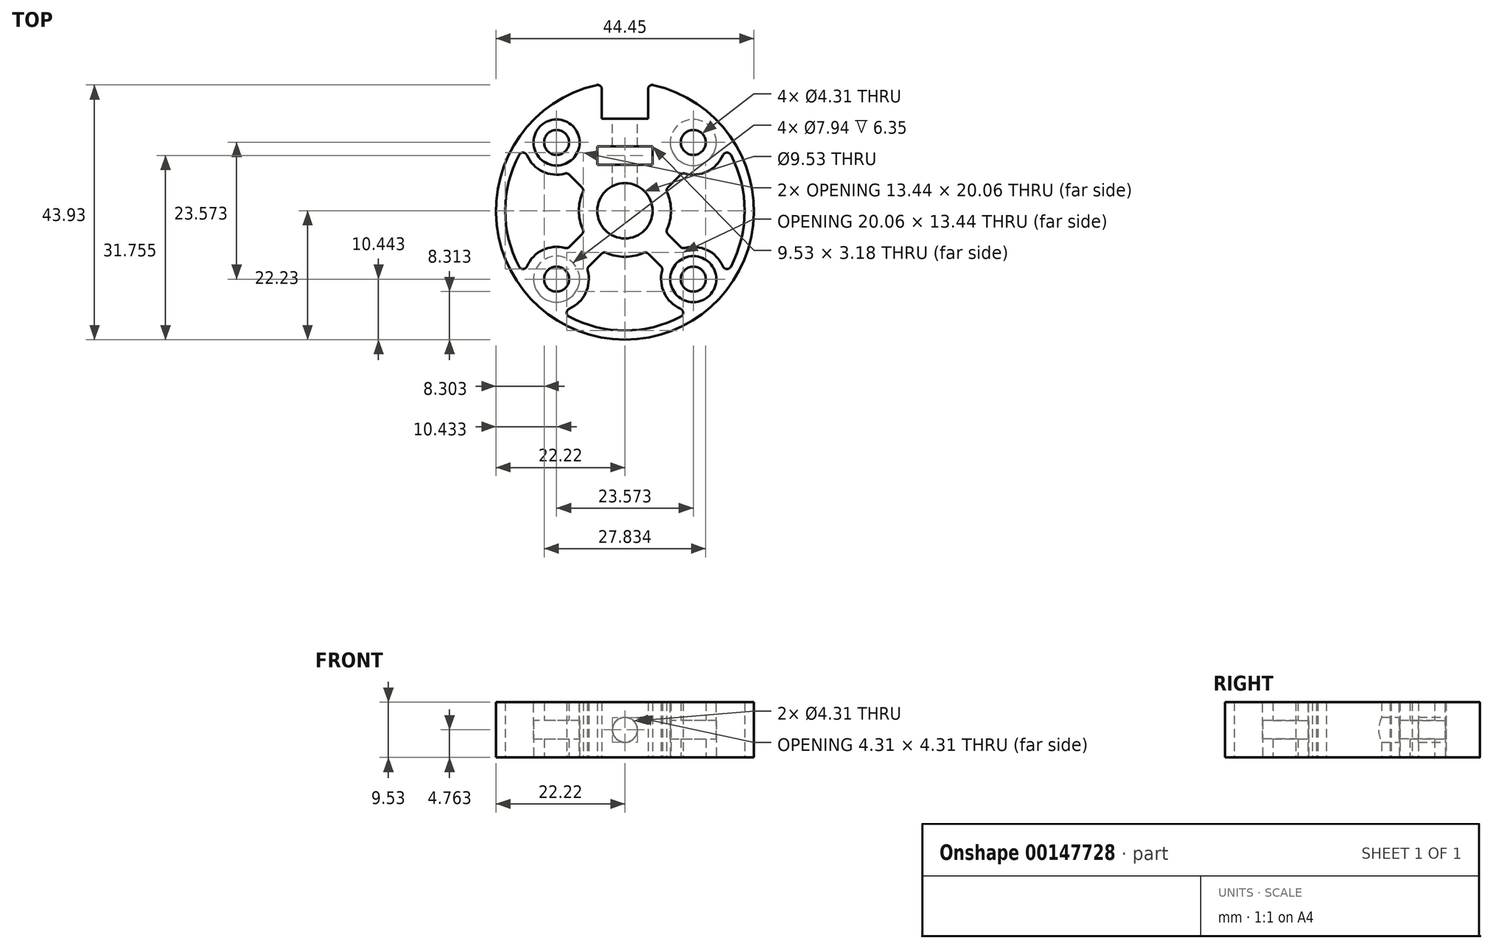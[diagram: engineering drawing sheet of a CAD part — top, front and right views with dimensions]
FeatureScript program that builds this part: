
annotation { "Feature Type Name" : "Feature", "Feature Type Description" : "" }
export const myFeature = defineFeature(function(context is Context, id is Id, definition is map)
    precondition{}
    {
        {
            var Q0;
            Q0=qCreatedBy(makeId("Top.planeOp"),FACE);
            var sketch = newSketch(context, id + "F0", { "sketchPlane" : qUnion([Q0])});
            skCircle(sketch, "E0", {"center": v(0, 0) * mm, "radius": 4.76 * mm});
            skLineSegment(sketch, "E1.bottom", {"start": v(11.79, 11.79) * mm, "end": v(-11.79, 11.79) * mm, "construction": true});
            skLineSegment(sketch, "E1.top", {"start": v(11.79, -11.79) * mm, "end": v(-11.79, -11.79) * mm, "construction": true});
            skLineSegment(sketch, "E1.left", {"start": v(11.79, 11.79) * mm, "end": v(11.79, -11.79) * mm, "construction": true});
            skLineSegment(sketch, "E1.right", {"start": v(-11.79, 11.79) * mm, "end": v(-11.79, -11.79) * mm, "construction": true});
            skCircle(sketch, "E2", {"center": v(-11.79, 11.79) * mm, "radius": 5.56 * mm, "construction": true});
            skLineSegment(sketch, "E3.bottom", {"start": v(-3.97, 21.87) * mm, "end": v(3.97, 21.87) * mm, "construction": true});
            skLineSegment(sketch, "E3.top", {"start": v(-3.97, 15.87) * mm, "end": v(3.97, 15.88) * mm});
            skLineSegment(sketch, "E3.left", {"start": v(-3.97, 21.87) * mm, "end": v(-3.97, 15.88) * mm});
            skLineSegment(sketch, "E3.right", {"start": v(3.97, 21.87) * mm, "end": v(3.97, 15.88) * mm});
            skArc(sketch, "E4", {"start": v(-3.97, 21.87) * mm, "mid": v(0, -22.22) * mm, "end": v(3.97, 21.87) * mm});
            skCircle(sketch, "E5", {"center": v(-11.79, 11.79) * mm, "radius": 2.15 * mm});
            skCircle(sketch, "E6", {"center": v(-11.79, -11.79) * mm, "radius": 2.15 * mm});
            skCircle(sketch, "E7", {"center": v(11.79, -11.79) * mm, "radius": 2.15 * mm});
            skCircle(sketch, "E8", {"center": v(11.79, 11.79) * mm, "radius": 2.15 * mm});
            skLineSegment(sketch, "E9", {"start": v(0, 15.88) * mm, "end": v(0, 11.11) * mm, "construction": true});
            skLineSegment(sketch, "E10", {"start": v(0, 0) * mm, "end": v(0, 3.17) * mm, "construction": true});
            skLineSegment(sketch, "E11", {"start": v(0, 3.17) * mm, "end": v(0, 4.76) * mm, "construction": true});
            skLineSegment(sketch, "E12", {"start": v(0, 4.76) * mm, "end": v(0, 7.94) * mm, "construction": true});
            skLineSegment(sketch, "E13.bottom", {"start": v(4.76, 11.11) * mm, "end": v(-4.76, 11.11) * mm});
            skLineSegment(sketch, "E13.top", {"start": v(4.76, 7.94) * mm, "end": v(-4.76, 7.94) * mm});
            skLineSegment(sketch, "E13.left", {"start": v(4.76, 11.11) * mm, "end": v(4.76, 7.94) * mm});
            skLineSegment(sketch, "E13.right", {"start": v(-4.76, 11.11) * mm, "end": v(-4.76, 7.94) * mm});
            skSolve(sketch);
        }
        {
            var Q0;
            Q0=qSketchRegion(id+"F0",true);
            extrude(context, id + "F1", {"entities" : qUnion([Q0]), "depth" : 9.52 * mm});
        }
        {
            var Q0;
            Q0=makeQuery(id+"F1.opExtrude","SWEPT_FACE",FACE,{"disambiguationData":[OSD([sQuery(id+"F0.wireOp",EDGE,"E3.top")])]});
            var sketch = newSketch(context, id + "F2", { "sketchPlane" : qUnion([Q0])});
            skLineSegment(sketch, "E14", {"start": v(0, 9.53) * mm, "end": v(0, 0) * mm, "construction": true});
            skCircle(sketch, "E15", {"center": v(0, 4.76) * mm, "radius": 2.15 * mm});
            skSolve(sketch);
        }
        {
            var Q0;
            Q0=qSketchRegion(id+"F2",true);
            var Q1;
            Q1=makeQuery(id+"F1.opExtrude","SWEPT_FACE",FACE,{"disambiguationData":[OSD([sQuery(id+"F0.wireOp",EDGE,"E0")])]});
            extrude(context, id + "F3", {"entities" : qUnion([Q0]), "operationType" : NewBodyOperationType.REMOVE, "endBound" : BoundingType.UP_TO_SURFACE, "oppositeDirection" : true, "endBoundEntityFace" : qUnion([Q1]), "depth" : 25.4 * mm});
        }
        {
            var Q0;
            Q0=makeQuery(id+"F1.opExtrude","CAP_FACE",FACE,{"disambiguationData":[OSD([sQuery(id+"F0.wireOp",EDGE,"E0"),sQuery(id+"F0.wireOp",EDGE,"E3.top"),sQuery(id+"F0.wireOp",EDGE,"E3.left"),sQuery(id+"F0.wireOp",EDGE,"E3.right"),sQuery(id+"F0.wireOp",EDGE,"E4"),sQuery(id+"F0.wireOp",EDGE,"E5"),sQuery(id+"F0.wireOp",EDGE,"E6"),sQuery(id+"F0.wireOp",EDGE,"E7"),sQuery(id+"F0.wireOp",EDGE,"E8")])],"isStart":true});
            cPlane(context, id + "F4", {"entities" : qUnion([Q0]), "cplaneType" : CPlaneType.OFFSET, "offset" : 3.17 * mm, "oppositeDirection" : true, "width" : 152.4 * mm, "height" : 152.4 * mm});
        }
        {
            var Q0;
            Q0=makeQuery(id+"F1.opExtrude","CAP_FACE",FACE,{"disambiguationData":[OSD([sQuery(id+"F0.wireOp",EDGE,"E0"),sQuery(id+"F0.wireOp",EDGE,"E3.top"),sQuery(id+"F0.wireOp",EDGE,"E3.left"),sQuery(id+"F0.wireOp",EDGE,"E3.right"),sQuery(id+"F0.wireOp",EDGE,"E4"),sQuery(id+"F0.wireOp",EDGE,"E5"),sQuery(id+"F0.wireOp",EDGE,"E6"),sQuery(id+"F0.wireOp",EDGE,"E7"),sQuery(id+"F0.wireOp",EDGE,"E8")])],"isStart":false});
            cPlane(context, id + "F5", {"entities" : qUnion([Q0]), "cplaneType" : CPlaneType.OFFSET, "offset" : 3.17 * mm, "oppositeDirection" : true, "width" : 152.4 * mm, "height" : 152.4 * mm});
        }
        {
            var Q0;
            Q0=makeQuery(id+"F1.opExtrude","CAP_FACE",FACE,{"disambiguationData":[OSD([sQuery(id+"F0.wireOp",EDGE,"E0"),sQuery(id+"F0.wireOp",EDGE,"E3.top"),sQuery(id+"F0.wireOp",EDGE,"E3.left"),sQuery(id+"F0.wireOp",EDGE,"E3.right"),sQuery(id+"F0.wireOp",EDGE,"E4"),sQuery(id+"F0.wireOp",EDGE,"E5"),sQuery(id+"F0.wireOp",EDGE,"E6"),sQuery(id+"F0.wireOp",EDGE,"E7"),sQuery(id+"F0.wireOp",EDGE,"E8")])],"isStart":true});
            var sketch = newSketch(context, id + "F6", { "sketchPlane" : qUnion([Q0])});
            skCircle(sketch, "E16", {"center": v(11.79, -11.79) * mm, "radius": 3.97 * mm});
            skCircle(sketch, "E17", {"center": v(-11.79, 11.79) * mm, "radius": 3.97 * mm});
            skSolve(sketch);
        }
        {
            var Q0;
            Q0=qSketchRegion(id+"F6",true);
            var Q1;
            Q1=qCreatedBy(id+"F5.planeOp",FACE);
            extrude(context, id + "F7", {"entities" : qUnion([Q0]), "operationType" : NewBodyOperationType.REMOVE, "endBound" : BoundingType.UP_TO_SURFACE, "oppositeDirection" : true, "endBoundEntityFace" : qUnion([Q1]), "depth" : 25.4 * mm});
        }
        {
            var Q0;
            Q0=makeQuery(id+"F1.opExtrude","CAP_FACE",FACE,{"disambiguationData":[OSD([sQuery(id+"F0.wireOp",EDGE,"E0"),sQuery(id+"F0.wireOp",EDGE,"E3.top"),sQuery(id+"F0.wireOp",EDGE,"E3.left"),sQuery(id+"F0.wireOp",EDGE,"E3.right"),sQuery(id+"F0.wireOp",EDGE,"E4"),sQuery(id+"F0.wireOp",EDGE,"E5"),sQuery(id+"F0.wireOp",EDGE,"E6"),sQuery(id+"F0.wireOp",EDGE,"E7"),sQuery(id+"F0.wireOp",EDGE,"E8")])],"isStart":true});
            var sketch = newSketch(context, id + "F8", { "sketchPlane" : qUnion([Q0])});
            skArc(sketch, "E18", {"start": v(-9.92, -6.55) * mm, "mid": v(-14.76, -7.1) * mm, "end": v(-17.31, -11.23) * mm});
            skArc(sketch, "E19", {"start": v(-17.31, 11.23) * mm, "mid": v(-14.76, 7.1) * mm, "end": v(-9.92, 6.55) * mm});
            skArc(sketch, "E20", {"start": v(-17.31, 11.23) * mm, "mid": v(-20.64, 0) * mm, "end": v(-17.31, -11.23) * mm});
            skLineSegment(sketch, "E21", {"start": v(-11.79, 11.79) * mm, "end": v(-8.24, 8.24) * mm, "construction": true});
            skLineSegment(sketch, "E22", {"start": v(-11.79, -11.79) * mm, "end": v(-8.24, -8.24) * mm, "construction": true});
            skLineSegment(sketch, "E23", {"start": v(0, 0) * mm, "end": v(-5.35, 5.35) * mm, "construction": true});
            skLineSegment(sketch, "E24", {"start": v(0, 0) * mm, "end": v(-5.35, -5.35) * mm, "construction": true});
            skLineSegment(sketch, "E25.bottom", {"start": v(-7.04, 3.67) * mm, "end": v(-9.92, 6.55) * mm});
            skLineSegment(sketch, "E25.top", {"start": v(-3.67, 7.04) * mm, "end": v(-6.55, 9.92) * mm, "construction": true});
            skLineSegment(sketch, "E25.left", {"start": v(-7.04, 3.67) * mm, "end": v(-3.67, 7.04) * mm, "construction": true});
            skLineSegment(sketch, "E25.right", {"start": v(-9.92, 6.55) * mm, "end": v(-6.55, 9.92) * mm, "construction": true});
            skLineSegment(sketch, "E26.bottom", {"start": v(-7.04, -3.67) * mm, "end": v(-9.92, -6.55) * mm});
            skLineSegment(sketch, "E26.top", {"start": v(-3.67, -7.04) * mm, "end": v(-6.55, -9.92) * mm, "construction": true});
            skLineSegment(sketch, "E26.left", {"start": v(-7.04, -3.67) * mm, "end": v(-3.67, -7.04) * mm, "construction": true});
            skLineSegment(sketch, "E26.right", {"start": v(-9.92, -6.55) * mm, "end": v(-6.55, -9.92) * mm, "construction": true});
            skArc(sketch, "E27", {"start": v(-7.04, 3.67) * mm, "mid": v(-7.94, 0) * mm, "end": v(-7.04, -3.67) * mm});
            skSolve(sketch);
        }
        {
            var Q0;
            Q0=qSketchRegion(id+"F8",true);
            var Q1;
            Q1=makeQuery(id+"F1.opExtrude","CAP_FACE",FACE,{"disambiguationData":[OSD([sQuery(id+"F0.wireOp",EDGE,"E0"),sQuery(id+"F0.wireOp",EDGE,"E3.top"),sQuery(id+"F0.wireOp",EDGE,"E3.left"),sQuery(id+"F0.wireOp",EDGE,"E3.right"),sQuery(id+"F0.wireOp",EDGE,"E4"),sQuery(id+"F0.wireOp",EDGE,"E5"),sQuery(id+"F0.wireOp",EDGE,"E6"),sQuery(id+"F0.wireOp",EDGE,"E7"),sQuery(id+"F0.wireOp",EDGE,"E8")])],"isStart":false});
            extrude(context, id + "F9", {"entities" : qUnion([Q0]), "operationType" : NewBodyOperationType.REMOVE, "endBound" : BoundingType.UP_TO_SURFACE, "oppositeDirection" : true, "endBoundEntityFace" : qUnion([Q1]), "depth" : 25.4 * mm});
        }
        {
            var Q0;
            Q0=makeQuery(id+"F9.boolean.opBoolean","COPY",EDGE,{"derivedFrom":makeQuery(id+"F9.opExtrude","SWEPT_EDGE",EDGE,{"disambiguationData":[OSD([sQuery(id+"F8.wireOp",EDGE,"E19"),sQuery(id+"F8.wireOp",EDGE,"E20")])]})});
            var Q1;
            Q1=makeQuery(id+"F9.boolean.opBoolean","COPY",EDGE,{"derivedFrom":makeQuery(id+"F9.opExtrude","SWEPT_EDGE",EDGE,{"disambiguationData":[OSD([sQuery(id+"F8.wireOp",EDGE,"E19"),sQuery(id+"F8.wireOp",EDGE,"E25.bottom")])]})});
            var Q2;
            Q2=makeQuery(id+"F9.boolean.opBoolean","COPY",EDGE,{"derivedFrom":makeQuery(id+"F9.opExtrude","SWEPT_EDGE",EDGE,{"disambiguationData":[OSD([sQuery(id+"F8.wireOp",EDGE,"E25.bottom"),sQuery(id+"F8.wireOp",EDGE,"E27")])]})});
            var Q3;
            Q3=makeQuery(id+"F9.boolean.opBoolean","COPY",EDGE,{"derivedFrom":makeQuery(id+"F9.opExtrude","SWEPT_EDGE",EDGE,{"disambiguationData":[OSD([sQuery(id+"F8.wireOp",EDGE,"E26.bottom"),sQuery(id+"F8.wireOp",EDGE,"E27")])]})});
            var Q4;
            Q4=makeQuery(id+"F9.boolean.opBoolean","COPY",EDGE,{"derivedFrom":makeQuery(id+"F9.opExtrude","SWEPT_EDGE",EDGE,{"disambiguationData":[OSD([sQuery(id+"F8.wireOp",EDGE,"E18"),sQuery(id+"F8.wireOp",EDGE,"E26.bottom")])]})});
            var Q5;
            Q5=makeQuery(id+"F9.boolean.opBoolean","COPY",EDGE,{"derivedFrom":makeQuery(id+"F9.opExtrude","SWEPT_EDGE",EDGE,{"disambiguationData":[OSD([sQuery(id+"F8.wireOp",EDGE,"E18"),sQuery(id+"F8.wireOp",EDGE,"E20")])]})});
            var Q6;
            Q6=makeQuery(id+"F1.opExtrude","SWEPT_EDGE",EDGE,{"disambiguationData":[OSD([sQuery(id+"F0.wireOp",EDGE,"E3.right"),sQuery(id+"F0.wireOp",EDGE,"E4")])]});
            var Q7;
            Q7=makeQuery(id+"F1.opExtrude","SWEPT_EDGE",EDGE,{"disambiguationData":[OSD([sQuery(id+"F0.wireOp",EDGE,"E3.left"),sQuery(id+"F0.wireOp",EDGE,"E4")])]});
            fillet(context, id + "F10", {"entities" : qUnion([Q0, Q1, Q2, Q3, Q4, Q5, Q6, Q7]), "radius" : 0.76 * mm, "tangentPropagation" : true, "allowEdgeOverflow" : false});
        }
        {
            var Q0;
            Q0=makeQuery(id+"F10.opFillet","BLEND_FACE",FACE,{"disambiguationData":[OSD([sQuery(id+"F8.wireOp",EDGE,"E19"),sQuery(id+"F8.wireOp",EDGE,"E25.bottom")])]});
            var Q1;
            Q1=makeQuery(id+"F9.boolean.opBoolean","COPY",FACE,{"derivedFrom":makeQuery(id+"F9.opExtrude","SWEPT_FACE",FACE,{"disambiguationData":[OSD([sQuery(id+"F8.wireOp",EDGE,"E25.bottom")])]})});
            var Q2;
            Q2=makeQuery(id+"F10.opFillet","BLEND_FACE",FACE,{"disambiguationData":[OSD([sQuery(id+"F8.wireOp",EDGE,"E25.bottom"),sQuery(id+"F8.wireOp",EDGE,"E27")])]});
            var Q3;
            Q3=makeQuery(id+"F9.boolean.opBoolean","COPY",FACE,{"derivedFrom":makeQuery(id+"F9.opExtrude","SWEPT_FACE",FACE,{"disambiguationData":[OSD([sQuery(id+"F8.wireOp",EDGE,"E27")])]})});
            var Q4;
            Q4=makeQuery(id+"F10.opFillet","BLEND_FACE",FACE,{"disambiguationData":[OSD([sQuery(id+"F8.wireOp",EDGE,"E26.bottom"),sQuery(id+"F8.wireOp",EDGE,"E27")])]});
            var Q5;
            Q5=makeQuery(id+"F9.boolean.opBoolean","COPY",FACE,{"derivedFrom":makeQuery(id+"F9.opExtrude","SWEPT_FACE",FACE,{"disambiguationData":[OSD([sQuery(id+"F8.wireOp",EDGE,"E26.bottom")])]})});
            var Q6;
            Q6=makeQuery(id+"F10.opFillet","BLEND_FACE",FACE,{"disambiguationData":[OSD([sQuery(id+"F8.wireOp",EDGE,"E18"),sQuery(id+"F8.wireOp",EDGE,"E26.bottom")])]});
            var Q7;
            Q7=makeQuery(id+"F9.boolean.opBoolean","COPY",FACE,{"derivedFrom":makeQuery(id+"F9.opExtrude","SWEPT_FACE",FACE,{"disambiguationData":[OSD([sQuery(id+"F8.wireOp",EDGE,"E18")])]})});
            var Q8;
            Q8=makeQuery(id+"F10.opFillet","BLEND_FACE",FACE,{"disambiguationData":[OSD([sQuery(id+"F8.wireOp",EDGE,"E18"),sQuery(id+"F8.wireOp",EDGE,"E20")])]});
            var Q9;
            Q9=makeQuery(id+"F9.boolean.opBoolean","COPY",FACE,{"derivedFrom":makeQuery(id+"F9.opExtrude","SWEPT_FACE",FACE,{"disambiguationData":[OSD([sQuery(id+"F8.wireOp",EDGE,"E20")])]})});
            var Q10;
            Q10=makeQuery(id+"F10.opFillet","BLEND_FACE",FACE,{"disambiguationData":[OSD([sQuery(id+"F8.wireOp",EDGE,"E19"),sQuery(id+"F8.wireOp",EDGE,"E20")])]});
            var Q11;
            Q11=makeQuery(id+"F9.boolean.opBoolean","COPY",FACE,{"derivedFrom":makeQuery(id+"F9.opExtrude","SWEPT_FACE",FACE,{"disambiguationData":[OSD([sQuery(id+"F8.wireOp",EDGE,"E19")])]})});
            var Q12;
            Q12=makeQuery(id+"F1.opExtrude","SWEPT_FACE",FACE,{"disambiguationData":[OSD([sQuery(id+"F0.wireOp",EDGE,"E0")])]});
            circularPattern(context, id + "F11", {"patternType" : PatternType.FACE, "faces" : qUnion([Q0, Q1, Q2, Q3, Q4, Q5, Q6, Q7, Q8, Q9, Q10, Q11]), "axis" : qUnion([Q12]), "angle" : 90 * degree, "instanceCount" : 3});
        }
        {
            var Q0;
            Q0=makeQuery(id+"F1.opExtrude","CAP_FACE",FACE,{"disambiguationData":[OSD([sQuery(id+"F0.wireOp",EDGE,"E0"),sQuery(id+"F0.wireOp",EDGE,"E3.top"),sQuery(id+"F0.wireOp",EDGE,"E3.left"),sQuery(id+"F0.wireOp",EDGE,"E3.right"),sQuery(id+"F0.wireOp",EDGE,"E4"),sQuery(id+"F0.wireOp",EDGE,"E5"),sQuery(id+"F0.wireOp",EDGE,"E6"),sQuery(id+"F0.wireOp",EDGE,"E7"),sQuery(id+"F0.wireOp",EDGE,"E8"),sQuery(id+"F0.wireOp",EDGE,"E13.bottom"),sQuery(id+"F0.wireOp",EDGE,"E13.top"),sQuery(id+"F0.wireOp",EDGE,"E13.left"),sQuery(id+"F0.wireOp",EDGE,"E13.right")])],"isStart":false});
            var sketch = newSketch(context, id + "F12", { "sketchPlane" : qUnion([Q0])});
            skCircle(sketch, "E28", {"center": v(11.79, -11.79) * mm, "radius": 3.97 * mm});
            skCircle(sketch, "E29", {"center": v(-11.79, 11.79) * mm, "radius": 3.97 * mm});
            skSolve(sketch);
        }
        {
            var Q0;
            Q0=qSketchRegion(id+"F12",true);
            var Q1;
            Q1=qCreatedBy(id+"F4.planeOp",FACE);
            extrude(context, id + "F13", {"entities" : qUnion([Q0]), "operationType" : NewBodyOperationType.REMOVE, "endBound" : BoundingType.UP_TO_SURFACE, "oppositeDirection" : true, "endBoundEntityFace" : qUnion([Q1]), "depth" : 25.4 * mm});
        }
    });
